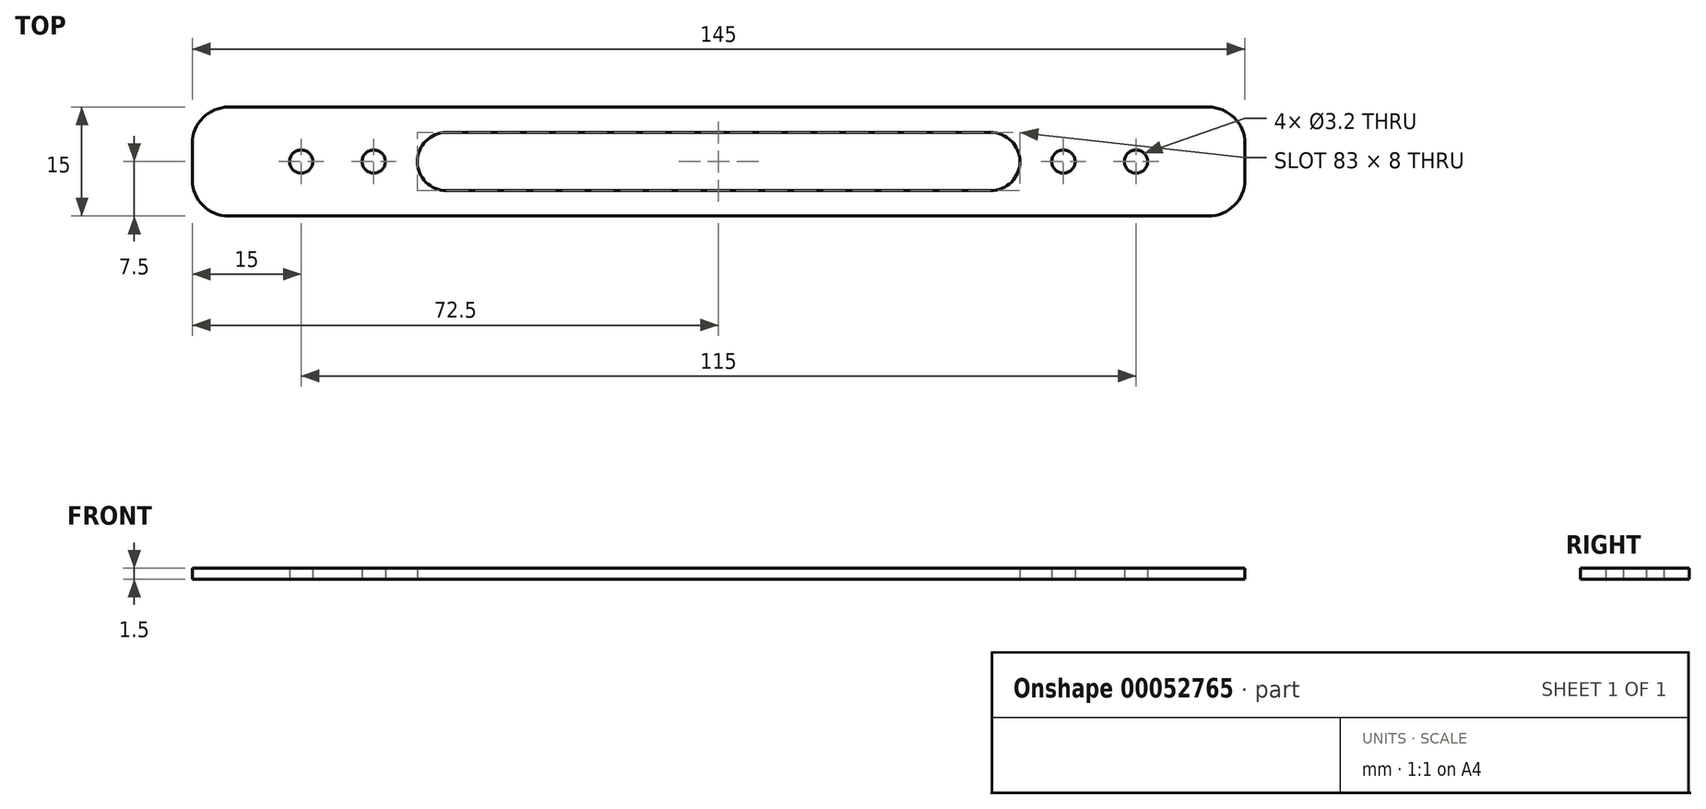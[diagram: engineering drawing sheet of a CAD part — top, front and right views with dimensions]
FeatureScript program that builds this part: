
annotation { "Feature Type Name" : "Feature", "Feature Type Description" : "" }
export const myFeature = defineFeature(function(context is Context, id is Id, definition is map)
    precondition{}
    {
        {
            var Q0;
            Q0=qCreatedBy(makeId("Top.planeOp"),FACE);
            var sketch = newSketch(context, id + "F0", { "sketchPlane" : qUnion([Q0])});
            skLineSegment(sketch, "E0", {"start": v(0, 17.88) * mm, "end": v(0, -17.88) * mm, "construction": true});
            skLineSegment(sketch, "E1", {"start": v(-56.64, 0) * mm, "end": v(71.93, 0) * mm, "construction": true});
            skLineSegment(sketch, "E2.0", {"start": v(-72.5, 17.88) * mm, "end": v(-72.5, -17.88) * mm, "construction": true});
            skLineSegment(sketch, "E3.0", {"start": v(72.5, 17.88) * mm, "end": v(72.5, -17.88) * mm, "construction": true});
            skLineSegment(sketch, "E4.0", {"start": v(-47.5, 17.88) * mm, "end": v(-47.5, -17.88) * mm, "construction": true});
            skLineSegment(sketch, "E5.0", {"start": v(-57.5, 17.88) * mm, "end": v(-57.5, -17.88) * mm, "construction": true});
            skLineSegment(sketch, "E6", {"start": v(-72.5, 0) * mm, "end": v(-65.92, 0) * mm, "construction": true});
            skPoint(sketch, "E6.endSnap0", {"position": v(-72.5, 0) * mm});
            skLineSegment(sketch, "E7.0", {"start": v(-72.5, -7.5) * mm, "end": v(-65.92, -7.5) * mm});
            skLineSegment(sketch, "E8.0", {"start": v(-72.5, 7.5) * mm, "end": v(-65.92, 7.5) * mm});
            skLineSegment(sketch, "E9", {"start": v(-72.5, 2.5) * mm, "end": v(-72.5, -2.5) * mm});
            skLineSegment(sketch, "E10", {"start": v(-67.5, 7.5) * mm, "end": v(72.5, 7.5) * mm});
            skLineSegment(sketch, "E11", {"start": v(72.5, 7.5) * mm, "end": v(72.5, -7.5) * mm});
            skLineSegment(sketch, "E12", {"start": v(72.5, -7.5) * mm, "end": v(-67.5, -7.5) * mm});
            skCircle(sketch, "E13", {"center": v(-57.5, 0) * mm, "radius": 1.6 * mm});
            skCircle(sketch, "E14", {"center": v(-47.5, 0) * mm, "radius": 1.6 * mm});
            skPoint(sketch, "E15.visualSharp", {"position": v(-72.5, 7.5) * mm});
            skArc(sketch, "E15.filletArc", {"start": v(-67.5, 7.5) * mm, "mid": v(-71.04, 6.04) * mm, "end": v(-72.5, 2.5) * mm});
            skPoint(sketch, "E16.visualSharp", {"position": v(-72.5, -7.5) * mm});
            skArc(sketch, "E16.filletArc", {"start": v(-72.5, -2.5) * mm, "mid": v(-71.04, -6.04) * mm, "end": v(-67.5, -7.5) * mm});
            skCircle(sketch, "E17.MirrorC", {"center": v(47.5, 0) * mm, "radius": 1.6 * mm});
            skCircle(sketch, "E18.MirrorC", {"center": v(57.5, 0) * mm, "radius": 1.6 * mm});
            skArc(sketch, "E19.MirrorCS", {"start": v(67.5, 7.5) * mm, "mid": v(71.04, 6.04) * mm, "end": v(72.5, 2.5) * mm});
            skArc(sketch, "E20.MirrorCS", {"start": v(72.5, -2.5) * mm, "mid": v(71.04, -6.04) * mm, "end": v(67.5, -7.5) * mm});
            skLineSegment(sketch, "E21.0", {"start": v(-37.5, 17.88) * mm, "end": v(-37.5, -17.88) * mm, "construction": true});
            skArc(sketch, "E22", {"start": v(-37.5, 4) * mm, "mid": v(-41.5, 0) * mm, "end": v(-37.5, -4) * mm});
            skLineSegment(sketch, "E23", {"start": v(-37.5, 4) * mm, "end": v(0, 4) * mm});
            skLineSegment(sketch, "E24", {"start": v(-37.5, -4) * mm, "end": v(0, -4) * mm});
            skLineSegment(sketch, "E25.MirrorCS", {"start": v(37.5, 4) * mm, "end": v(0, 4) * mm});
            skArc(sketch, "E26.MirrorC", {"start": v(37.5, 4) * mm, "mid": v(41.5, 0) * mm, "end": v(37.5, -4) * mm});
            skLineSegment(sketch, "E27.MirrorCS", {"start": v(37.5, -4) * mm, "end": v(0, -4) * mm});
            skSolve(sketch);
        }
        {
            var Q0;
            Q0=makeQuery(id+"F0.imprint","IMPRINT",FACE,{"disambiguationData":[TD([[makeQuery(id+"F0.imprint","IMPRINT",EDGE,{"derivedFrom":sQuery(id+"F0.wireOp",EDGE,"E9")}),1.0]])]});
            extrude(context, id + "F1", {"entities" : qUnion([Q0]), "depth" : 1.5 * mm});
        }
    });
